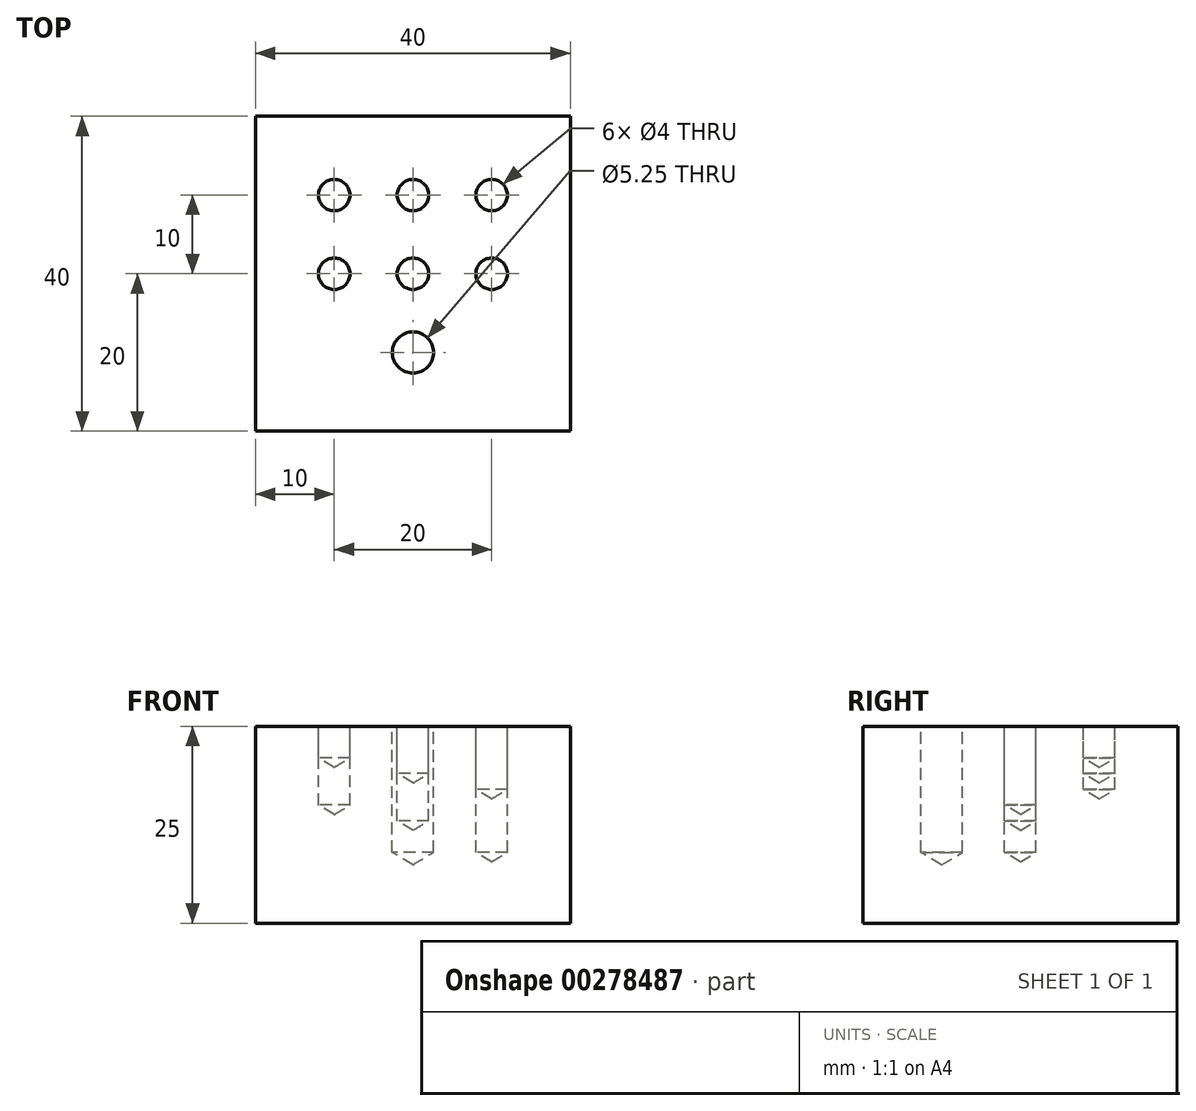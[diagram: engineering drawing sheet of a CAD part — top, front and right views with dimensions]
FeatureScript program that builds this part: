
annotation { "Feature Type Name" : "Feature", "Feature Type Description" : "" }
export const myFeature = defineFeature(function(context is Context, id is Id, definition is map)
    precondition{}
    {
        {
            var Q0;
            Q0=qCreatedBy(makeId("Top.planeOp"),FACE);
            var sketch = newSketch(context, id + "F0", { "sketchPlane" : qUnion([Q0])});
            skLineSegment(sketch, "E0.bottom", {"start": v(20, 20) * mm, "end": v(-20, 20) * mm});
            skLineSegment(sketch, "E0.top", {"start": v(20, -20) * mm, "end": v(-20, -20) * mm});
            skLineSegment(sketch, "E0.left", {"start": v(20, 20) * mm, "end": v(20, -20) * mm});
            skLineSegment(sketch, "E0.right", {"start": v(-20, 20) * mm, "end": v(-20, -20) * mm});
            skPoint(sketch, "E0.middle", {"position": v(0, 0) * mm});
            skSolve(sketch);
        }
        {
            var Q0;
            Q0=makeQuery(id+"F0.imprint","IMPRINT",FACE,{"disambiguationData":[TD([[makeQuery(id+"F0.imprint","IMPRINT",EDGE,{"derivedFrom":sQuery(id+"F0.wireOp",EDGE,"E0.bottom")}),1.0]])]});
            extrude(context, id + "F1", {"entities" : qUnion([Q0]), "depth" : 25 * mm});
        }
        {
            var Q0;
            Q0=makeQuery(id+"F1.opExtrude","CAP_FACE",FACE,{"disambiguationData":[OSD([sQuery(id+"F0.wireOp",EDGE,"E0.bottom"),sQuery(id+"F0.wireOp",EDGE,"E0.top"),sQuery(id+"F0.wireOp",EDGE,"E0.left"),sQuery(id+"F0.wireOp",EDGE,"E0.right")])],"isStart":false});
            var sketch = newSketch(context, id + "F2", { "sketchPlane" : qUnion([Q0])});
            skPoint(sketch, "E1", {"position": v(-10, 10) * mm});
            skPoint(sketch, "E2.0.1.0", {"position": v(-10, 0) * mm});
            skPoint(sketch, "E2.1.0.0", {"position": v(0, 10) * mm});
            skPoint(sketch, "E2.1.1.0", {"position": v(0, 0) * mm});
            skPoint(sketch, "E2.2.0.0", {"position": v(10, 10) * mm});
            skPoint(sketch, "E2.2.1.0", {"position": v(10, 0) * mm});
            skLineSegment(sketch, "E2.direction1", {"start": v(-10, 10) * mm, "end": v(0, 10) * mm, "construction": true});
            skLineSegment(sketch, "E2.direction2", {"start": v(-10, 10) * mm, "end": v(-10, 0) * mm, "construction": true});
            skPoint(sketch, "E3", {"position": v(0, -10) * mm});
            skSolve(sketch);
        }
        {
            var Q0;
            Q0=sQuery(id+"F2.wireOp",VERTEX,"E1");
            var Q1;
            Q1=makeQuery(id+"F1.opExtrude","SWEPT_BODY",BODY,{"disambiguationData":[OSD([sQuery(id+"F0.wireOp",EDGE,"E0.bottom"),sQuery(id+"F0.wireOp",EDGE,"E0.top"),sQuery(id+"F0.wireOp",EDGE,"E0.left"),sQuery(id+"F0.wireOp",EDGE,"E0.right")])]});
            hole(context, id + "F3", {"style" : HoleStyle.SIMPLE, "endStyle" : HoleEndStyle.BLIND, "holeDiameter" : 4 * mm, "holeDepth" : 4 * mm, "tappedDepth" : 12 * mm, "tapClearance" : 3, "locations" : qUnion([Q0]), "scope" : qUnion([Q1])});
        }
        {
            var Q0;
            Q0=sQuery(id+"F2.wireOp",VERTEX,"E2.1.0.0");
            var Q1;
            Q1=makeQuery(id+"F1.opExtrude","SWEPT_BODY",BODY,{"disambiguationData":[OSD([sQuery(id+"F0.wireOp",EDGE,"E0.bottom"),sQuery(id+"F0.wireOp",EDGE,"E0.top"),sQuery(id+"F0.wireOp",EDGE,"E0.left"),sQuery(id+"F0.wireOp",EDGE,"E0.right")])]});
            hole(context, id + "F4", {"style" : HoleStyle.SIMPLE, "endStyle" : HoleEndStyle.BLIND, "holeDiameter" : 4 * mm, "holeDepth" : 6 * mm, "tappedDepth" : 12 * mm, "tapClearance" : 3, "locations" : qUnion([Q0]), "scope" : qUnion([Q1])});
        }
        {
            var Q0;
            Q0=sQuery(id+"F2.wireOp",VERTEX,"E2.2.0.0");
            var Q1;
            Q1=makeQuery(id+"F1.opExtrude","SWEPT_BODY",BODY,{"disambiguationData":[OSD([sQuery(id+"F0.wireOp",EDGE,"E0.bottom"),sQuery(id+"F0.wireOp",EDGE,"E0.top"),sQuery(id+"F0.wireOp",EDGE,"E0.left"),sQuery(id+"F0.wireOp",EDGE,"E0.right")])]});
            hole(context, id + "F5", {"style" : HoleStyle.SIMPLE, "endStyle" : HoleEndStyle.BLIND, "holeDiameter" : 4 * mm, "holeDepth" : 8 * mm, "tappedDepth" : 12 * mm, "tapClearance" : 3, "locations" : qUnion([Q0]), "scope" : qUnion([Q1])});
        }
        {
            var Q0;
            Q0=sQuery(id+"F2.wireOp",VERTEX,"E2.0.1.0");
            var Q1;
            Q1=makeQuery(id+"F1.opExtrude","SWEPT_BODY",BODY,{"disambiguationData":[OSD([sQuery(id+"F0.wireOp",EDGE,"E0.bottom"),sQuery(id+"F0.wireOp",EDGE,"E0.top"),sQuery(id+"F0.wireOp",EDGE,"E0.left"),sQuery(id+"F0.wireOp",EDGE,"E0.right")])]});
            hole(context, id + "F6", {"style" : HoleStyle.SIMPLE, "endStyle" : HoleEndStyle.BLIND, "holeDiameter" : 4 * mm, "holeDepth" : 10 * mm, "tappedDepth" : 12 * mm, "tapClearance" : 3, "locations" : qUnion([Q0]), "scope" : qUnion([Q1])});
        }
        {
            var Q0;
            Q0=sQuery(id+"F2.wireOp",VERTEX,"E2.1.1.0");
            var Q1;
            Q1=makeQuery(id+"F1.opExtrude","SWEPT_BODY",BODY,{"disambiguationData":[OSD([sQuery(id+"F0.wireOp",EDGE,"E0.bottom"),sQuery(id+"F0.wireOp",EDGE,"E0.top"),sQuery(id+"F0.wireOp",EDGE,"E0.left"),sQuery(id+"F0.wireOp",EDGE,"E0.right")])]});
            hole(context, id + "F7", {"style" : HoleStyle.SIMPLE, "endStyle" : HoleEndStyle.BLIND, "holeDiameter" : 4 * mm, "holeDepth" : 12 * mm, "tappedDepth" : 12 * mm, "tapClearance" : 3, "locations" : qUnion([Q0]), "scope" : qUnion([Q1])});
        }
        {
            var Q0;
            Q0=sQuery(id+"F2.wireOp",VERTEX,"E2.2.1.0");
            var Q1;
            Q1=makeQuery(id+"F1.opExtrude","SWEPT_BODY",BODY,{"disambiguationData":[OSD([sQuery(id+"F0.wireOp",EDGE,"E0.bottom"),sQuery(id+"F0.wireOp",EDGE,"E0.top"),sQuery(id+"F0.wireOp",EDGE,"E0.left"),sQuery(id+"F0.wireOp",EDGE,"E0.right")])]});
            hole(context, id + "F8", {"style" : HoleStyle.SIMPLE, "endStyle" : HoleEndStyle.BLIND, "holeDiameter" : 4 * mm, "holeDepth" : 16 * mm, "tappedDepth" : 12 * mm, "tapClearance" : 3, "locations" : qUnion([Q0]), "scope" : qUnion([Q1])});
        }
        {
            var Q0;
            Q0=sQuery(id+"F2.wireOp",VERTEX,"E3");
            var Q1;
            Q1=makeQuery(id+"F1.opExtrude","SWEPT_BODY",BODY,{"disambiguationData":[OSD([sQuery(id+"F0.wireOp",EDGE,"E0.bottom"),sQuery(id+"F0.wireOp",EDGE,"E0.top"),sQuery(id+"F0.wireOp",EDGE,"E0.left"),sQuery(id+"F0.wireOp",EDGE,"E0.right")])]});
            hole(context, id + "F9", {"style" : HoleStyle.SIMPLE, "endStyle" : HoleEndStyle.BLIND, "standardTappedOrClearance" : lookupTablePath({ "standard" : "ISO", "fit" : "Close", "size" : "M5", "type" : "Clearance" }), "standardBlindInLast" : lookupTablePath({ "fit" : "Close", "standard" : "ISO", "size" : "M5", "type" : "Clearance" }), "holeDiameter" : 5.25 * mm, "holeDepth" : 16 * mm, "tappedDepth" : 12 * mm, "tapClearance" : 3, "locations" : qUnion([Q0]), "scope" : qUnion([Q1])});
        }
    });
